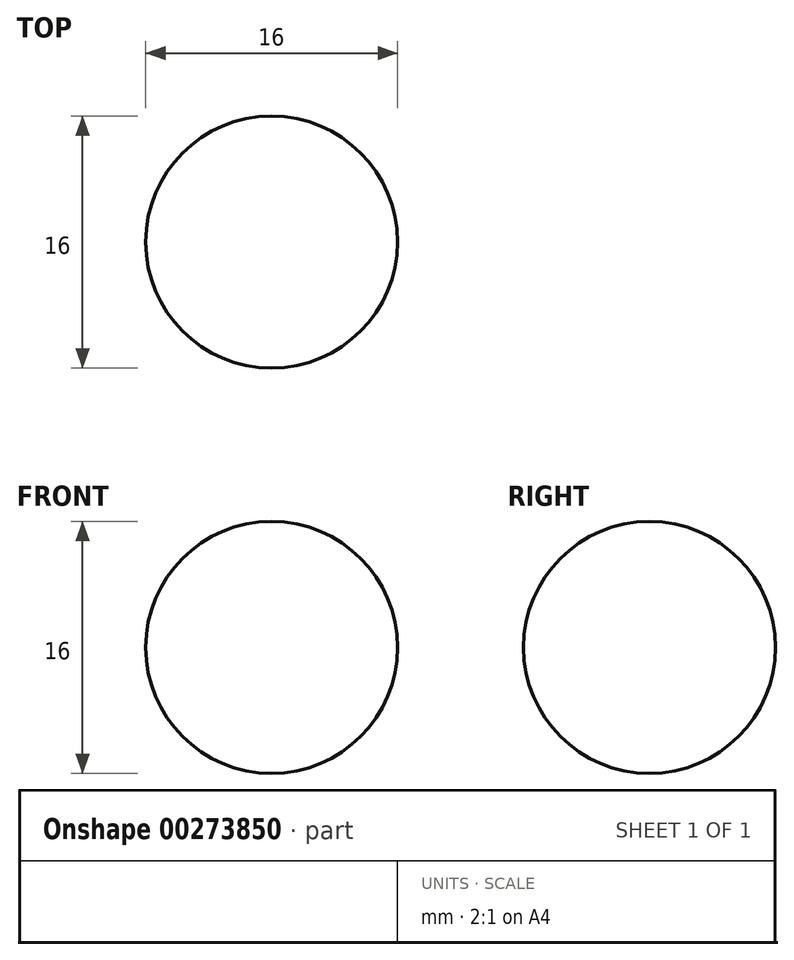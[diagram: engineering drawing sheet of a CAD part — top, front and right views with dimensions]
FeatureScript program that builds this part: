
annotation { "Feature Type Name" : "Feature", "Feature Type Description" : "" }
export const myFeature = defineFeature(function(context is Context, id is Id, definition is map)
    precondition{}
    {
        {
            var Q0;
            Q0=qCreatedBy(makeId("Front.planeOp"),FACE);
            var sketch = newSketch(context, id + "F0", { "sketchPlane" : qUnion([Q0])});
            skCircle(sketch, "E0", {"center": v(0, 0) * mm, "radius": 8 * mm});
            skLineSegment(sketch, "E1", {"start": v(0, 0) * mm, "end": v(0, 20.85) * mm, "construction": true});
            skLineSegment(sketch, "E2", {"start": v(0, 0) * mm, "end": v(0, -11.79) * mm});
            skLineSegment(sketch, "E3", {"start": v(0, -11.79) * mm, "end": v(0, 11.12) * mm});
            skSolve(sketch);
        }
        {
            var Q0;
            {var subQ0=sQuery(id+"F0.wireOp",EDGE,"E3");var subQ4=makeQuery(id+"F0.imprint","IMPRINT",VERTEX,{"derivedFrom":subQ0});Q0=makeQuery(id+"F0.imprint","IMPRINT",FACE,{"disambiguationData":[TD([[makeQuery(id+"F0.imprint","IMPRINT",EDGE,{"disambiguationData":[TD([[subQ4,1.0]])],"derivedFrom":subQ0}),1.0]])]});}
            var Q1;
            Q1=sQuery(id+"F0.wireOp",EDGE,"E1");
            revolve(context, id + "F1", {"entities" : qUnion([Q0]), "axis" : qUnion([Q1]), "revolveType" : RevolveType.FULL});
        }
    });
